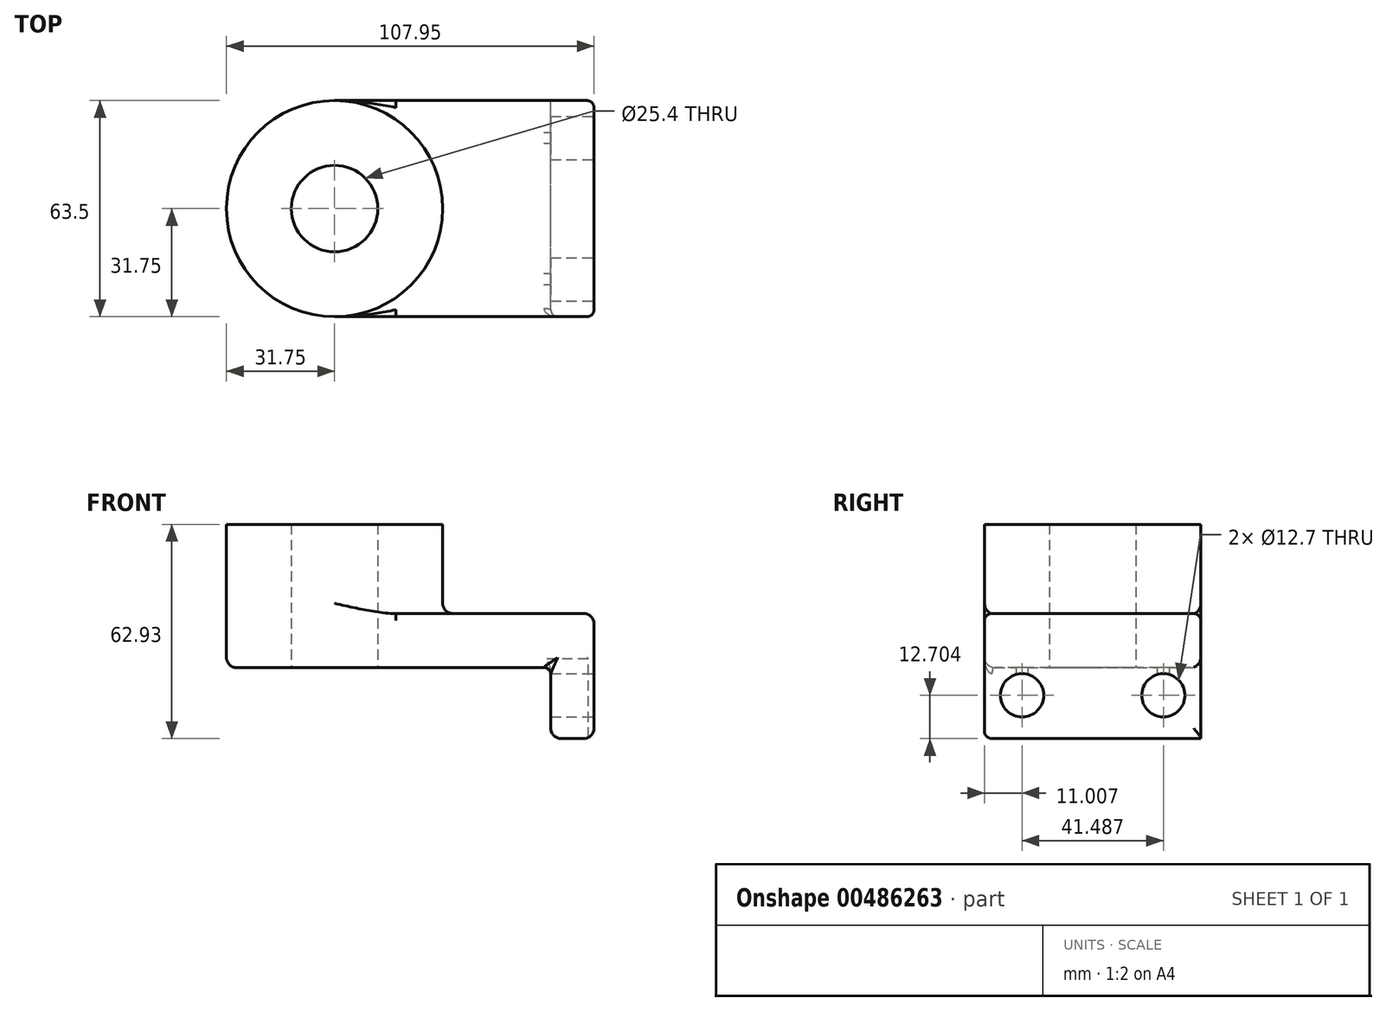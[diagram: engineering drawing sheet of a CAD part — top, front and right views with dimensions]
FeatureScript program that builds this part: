
annotation { "Feature Type Name" : "Feature", "Feature Type Description" : "" }
export const myFeature = defineFeature(function(context is Context, id is Id, definition is map)
    precondition{}
    {
        {
            var Q0;
            Q0=qCreatedBy(makeId("Top.planeOp"),FACE);
            var sketch = newSketch(context, id + "F0", { "sketchPlane" : qUnion([Q0])});
            skLineSegment(sketch, "E0.bottom", {"start": v(38.1, 31.75) * mm, "end": v(-38.1, 31.75) * mm});
            skLineSegment(sketch, "E0.top", {"start": v(38.1, -31.75) * mm, "end": v(-38.1, -31.75) * mm});
            skLineSegment(sketch, "E0.left", {"start": v(38.1, 31.75) * mm, "end": v(38.1, -31.75) * mm});
            skLineSegment(sketch, "E0.right", {"start": v(-38.1, 31.75) * mm, "end": v(-38.1, -31.75) * mm});
            skPoint(sketch, "E0.middle", {"position": v(0, 0) * mm});
            skCircle(sketch, "E1", {"center": v(-38.1, 0) * mm, "radius": 31.75 * mm});
            skCircle(sketch, "E2", {"center": v(-38.1, 0) * mm, "radius": 12.7 * mm});
            skSolve(sketch);
        }
        {
            var Q0;
            {var subQ1=sQuery(id+"F0.wireOp",EDGE,"E0.right");var subQ3=sQuery(id+"F0.wireOp",EDGE,"E2");var subQ4=makeQuery(id+"F0.imprint","INTERSECT",VERTEX,{"disambiguationData":[OD(0.0)],"derivedFrom":[subQ1,subQ3]});Q0=makeQuery(id+"F0.imprint","IMPRINT",FACE,{"disambiguationData":[TD([[makeQuery(id+"F0.imprint","IMPRINT",EDGE,{"disambiguationData":[TD([[subQ4,-1.0]])],"derivedFrom":subQ3}),-1.0]])]});}
            var Q1;
            {var subQ1=sQuery(id+"F0.wireOp",EDGE,"E0.right");var subQ3=sQuery(id+"F0.wireOp",EDGE,"E2");var subQ4=makeQuery(id+"F0.imprint","INTERSECT",VERTEX,{"disambiguationData":[OD(0.0)],"derivedFrom":[subQ1,subQ3]});Q1=makeQuery(id+"F0.imprint","IMPRINT",FACE,{"disambiguationData":[TD([[makeQuery(id+"F0.imprint","IMPRINT",EDGE,{"disambiguationData":[TD([[subQ4,1.0]])],"derivedFrom":subQ3}),-1.0]])]});}
            var Q2;
            {var subQ0=sQuery(id+"F0.wireOp",EDGE,"E0.bottom");Q2=makeQuery(id+"F0.imprint","IMPRINT",FACE,{"disambiguationData":[TD([[makeQuery(id+"F0.imprint","IMPRINT",EDGE,{"derivedFrom":subQ0}),1.0]])]});}
            extrude(context, id + "F1", {"entities" : qUnion([Q0, Q1, Q2]), "depth" : 15.9 * mm});
        }
        {
            var Q0;
            {var subQ1=sQuery(id+"F0.wireOp",EDGE,"E0.right");var subQ3=sQuery(id+"F0.wireOp",EDGE,"E2");var subQ4=makeQuery(id+"F0.imprint","INTERSECT",VERTEX,{"disambiguationData":[OD(0.0)],"derivedFrom":[subQ1,subQ3]});Q0=makeQuery(id+"F0.imprint","IMPRINT",FACE,{"disambiguationData":[TD([[makeQuery(id+"F0.imprint","IMPRINT",EDGE,{"disambiguationData":[TD([[subQ4,1.0]])],"derivedFrom":subQ3}),-1.0]])]});}
            var Q1;
            {var subQ1=sQuery(id+"F0.wireOp",EDGE,"E0.right");var subQ3=sQuery(id+"F0.wireOp",EDGE,"E2");var subQ4=makeQuery(id+"F0.imprint","INTERSECT",VERTEX,{"disambiguationData":[OD(0.0)],"derivedFrom":[subQ1,subQ3]});Q1=makeQuery(id+"F0.imprint","IMPRINT",FACE,{"disambiguationData":[TD([[makeQuery(id+"F0.imprint","IMPRINT",EDGE,{"disambiguationData":[TD([[subQ4,-1.0]])],"derivedFrom":subQ3}),-1.0]])]});}
            extrude(context, id + "F2", {"entities" : qUnion([Q0, Q1]), "operationType" : NewBodyOperationType.ADD, "depth" : 42.1 * mm});
        }
        {
            var Q0;
            Q0=makeQuery(id+"F1.opExtrude","SWEPT_FACE",FACE,{"disambiguationData":[OSD([sQuery(id+"F0.wireOp",EDGE,"E0.left")])]});
            var sketch = newSketch(context, id + "F3", { "sketchPlane" : qUnion([Q0])});
            skLineSegment(sketch, "E3.bottom", {"start": v(-31.75, 15.9) * mm, "end": v(31.72, 15.9) * mm});
            skLineSegment(sketch, "E3.top", {"start": v(-31.75, -20.83) * mm, "end": v(31.72, -20.83) * mm});
            skLineSegment(sketch, "E3.left", {"start": v(-31.75, 15.9) * mm, "end": v(-31.75, -20.83) * mm});
            skLineSegment(sketch, "E3.right", {"start": v(31.72, 15.9) * mm, "end": v(31.72, -20.83) * mm});
            skCircle(sketch, "E4", {"center": v(-20.74, -8.13) * mm, "radius": 6.35 * mm});
            skCircle(sketch, "E5.MirrorC", {"center": v(20.74, -8.13) * mm, "radius": 6.35 * mm});
            skSolve(sketch);
        }
        {
            var Q0;
            Q0 = qSketchRegion(id + "F3", true);
            extrude(context, id + "F4", {"entities" : qUnion([Q0]), "operationType" : NewBodyOperationType.ADD, "oppositeDirection" : true, "depth" : 12.7 * mm});
        }
        {
            var Q0;
            Q0=makeQuery(id+"F1.opExtrude","CAP_EDGE",EDGE,{"disambiguationData":[OSD([sQuery(id+"F0.wireOp",EDGE,"E0.left")])],"isStart":false});
            var Q1;
            {var subQ0=sQuery(id+"F0.wireOp",EDGE,"E1");Q1=makeQuery(id+"F2.boolean.opBoolean","INTERSECT",EDGE,{"derivedFrom":[makeQuery(id+"F1.opExtrude","CAP_FACE",FACE,{"disambiguationData":[OSD([sQuery(id+"F0.wireOp",EDGE,"E0.bottom"),sQuery(id+"F0.wireOp",EDGE,"E0.top"),sQuery(id+"F0.wireOp",EDGE,"E0.left"),subQ0,sQuery(id+"F0.wireOp",EDGE,"E2")])],"isStart":false}),makeQuery(id+"F2.opExtrude","SWEPT_FACE",FACE,{"disambiguationData":[OSD([subQ0])]})]});}
            var Q2;
            Q2=makeQuery(id+"F4.opExtrude","CAP_EDGE",EDGE,{"disambiguationData":[OSD([sQuery(id+"F3.wireOp",EDGE,"E3.top")])],"isStart":false});
            var Q3;
            Q3=makeQuery(id+"F4.opExtrude","CAP_EDGE",EDGE,{"disambiguationData":[OSD([sQuery(id+"F3.wireOp",EDGE,"E3.top")])],"isStart":true});
            var Q4;
            Q4=makeQuery(id+"F1.opExtrude","CAP_EDGE",EDGE,{"disambiguationData":[OSD([sQuery(id+"F0.wireOp",EDGE,"E0.bottom")])],"isStart":true});
            fillet(context, id + "F5", {"entities" : qUnion([Q0, Q1, Q2, Q3, Q4]), "radius" : 3 * mm, "tangentPropagation" : true, "allowEdgeOverflow" : false});
        }
        {
            var Q0;
            {var subQ0=sQuery(id+"F0.wireOp",EDGE,"E0.top");var subQ1=sQuery(id+"F0.wireOp",EDGE,"E1");Q0=makeQuery(id+"F5.opFillet","BLEND_EDGE",EDGE,{"blendedFrom":[makeQuery(id+"F2.boolean.opBoolean","INTERSECT",EDGE,{"derivedFrom":[makeQuery(id+"F1.opExtrude","CAP_FACE",FACE,{"disambiguationData":[OSD([sQuery(id+"F0.wireOp",EDGE,"E0.bottom"),subQ0,sQuery(id+"F0.wireOp",EDGE,"E0.left"),subQ1,sQuery(id+"F0.wireOp",EDGE,"E2")])],"isStart":false}),makeQuery(id+"F2.opExtrude","SWEPT_FACE",FACE,{"disambiguationData":[OSD([subQ1])]})]}),makeQuery(id+"F4.boolean.opBoolean","MERGE",FACE,{"derivedFrom":[makeQuery(id+"F1.opExtrude","SWEPT_FACE",FACE,{"disambiguationData":[OSD([subQ0])]}),makeQuery(id+"F4.opExtrude","SWEPT_FACE",FACE,{"disambiguationData":[OSD([sQuery(id+"F3.wireOp",EDGE,"E3.left")])]})]})],"blendedInto":[makeQuery(id+"F4.boolean.opBoolean","MERGE",FACE,{"derivedFrom":[makeQuery(id+"F1.opExtrude","SWEPT_FACE",FACE,{"disambiguationData":[OSD([subQ0])]}),makeQuery(id+"F4.opExtrude","SWEPT_FACE",FACE,{"disambiguationData":[OSD([sQuery(id+"F3.wireOp",EDGE,"E3.left")])]})]})]});}
            var Q1;
            Q1=makeQuery(id+"F1.opExtrude","CAP_EDGE",EDGE,{"disambiguationData":[OSD([sQuery(id+"F0.wireOp",EDGE,"E0.top")])],"isStart":false});
            var Q2;
            Q2=makeQuery(id+"F1.opExtrude","CAP_EDGE",EDGE,{"disambiguationData":[OSD([sQuery(id+"F0.wireOp",EDGE,"E0.bottom")])],"isStart":false});
            fillet(context, id + "F6", {"entities" : qUnion([Q0, Q1, Q2]), "radius" : 2.06 * mm, "tangentPropagation" : true, "allowEdgeOverflow" : false});
        }
        {
            var Q0;
            Q0=makeQuery(id+"F4.boolean.opBoolean","INTERSECT",EDGE,{"derivedFrom":[makeQuery(id+"F1.opExtrude","CAP_FACE",FACE,{"disambiguationData":[OSD([sQuery(id+"F0.wireOp",EDGE,"E0.bottom"),sQuery(id+"F0.wireOp",EDGE,"E0.top"),sQuery(id+"F0.wireOp",EDGE,"E0.left"),sQuery(id+"F0.wireOp",EDGE,"E1"),sQuery(id+"F0.wireOp",EDGE,"E2")])],"isStart":true}),makeQuery(id+"F4.opExtrude","CAP_FACE",FACE,{"disambiguationData":[OSD([sQuery(id+"F3.wireOp",EDGE,"E3.bottom"),sQuery(id+"F3.wireOp",EDGE,"E3.top"),sQuery(id+"F3.wireOp",EDGE,"E3.left"),sQuery(id+"F3.wireOp",EDGE,"E3.right"),sQuery(id+"F3.wireOp",EDGE,"E4"),sQuery(id+"F3.wireOp",EDGE,"E5.MirrorC")])],"isStart":false})]});
            fillet(context, id + "F7", {"entities" : qUnion([Q0]), "radius" : 2 * mm, "tangentPropagation" : true, "allowEdgeOverflow" : false});
        }
    });
